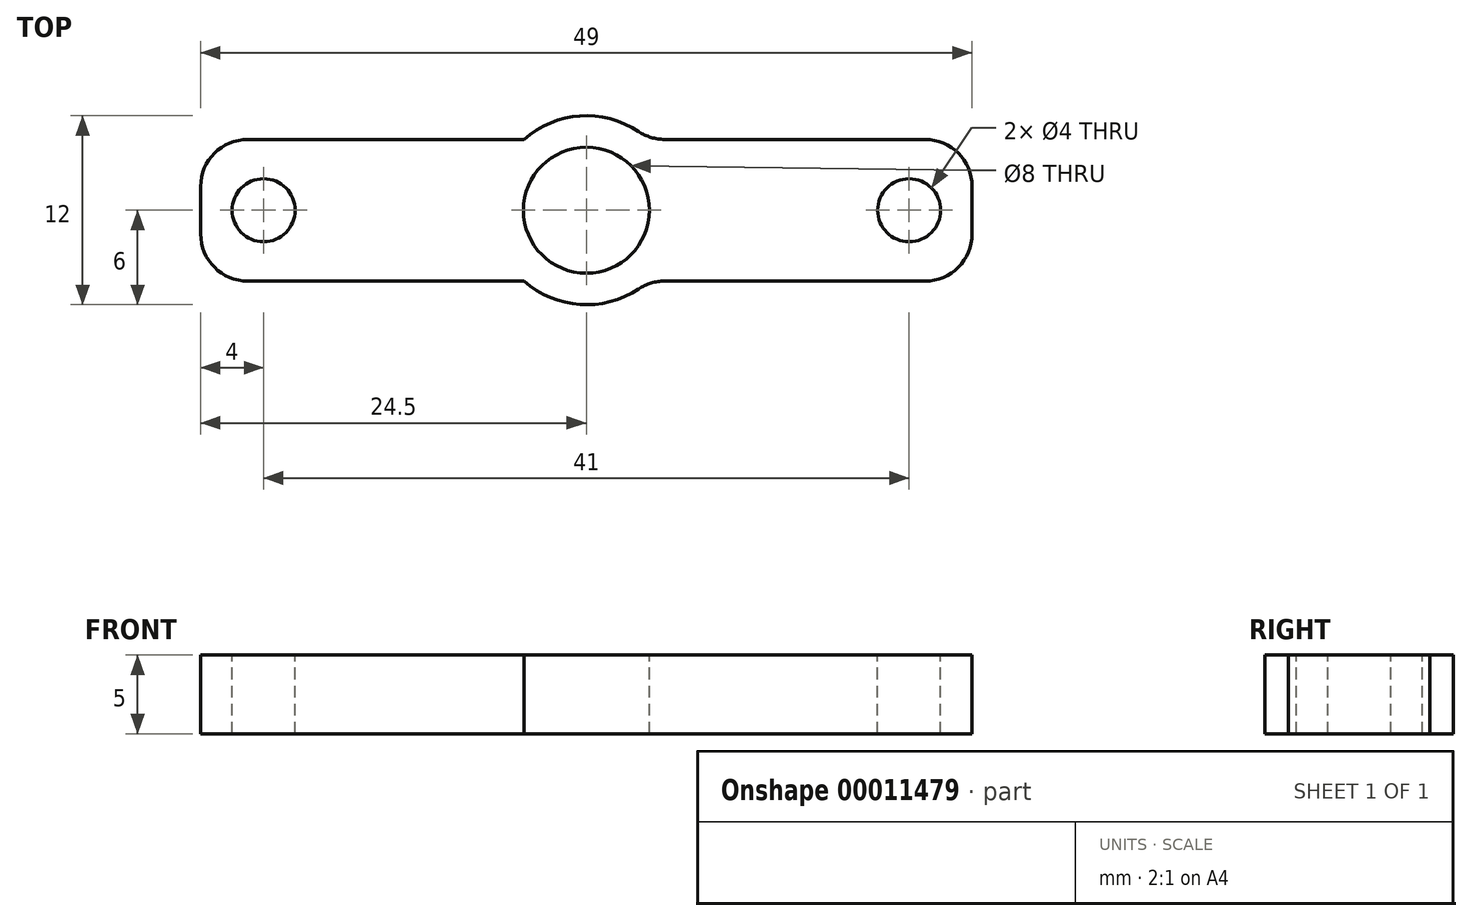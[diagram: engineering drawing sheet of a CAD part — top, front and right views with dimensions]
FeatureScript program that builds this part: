
annotation { "Feature Type Name" : "Feature", "Feature Type Description" : "" }
export const myFeature = defineFeature(function(context is Context, id is Id, definition is map)
    precondition{}
    {
        {
            var Q0;
            Q0=qCreatedBy(makeId("Top.planeOp"),FACE);
            var sketch = newSketch(context, id + "F0", { "sketchPlane" : qUnion([Q0])});
            skLineSegment(sketch, "E0.rect.bottom", {"start": v(24.5, 4.5) * mm, "end": v(3.97, 4.5) * mm});
            skLineSegment(sketch, "E0.rect.top", {"start": v(24.5, -4.5) * mm, "end": v(3.97, -4.5) * mm});
            skLineSegment(sketch, "E0.rect.left", {"start": v(24.5, 4.5) * mm, "end": v(24.5, -4.5) * mm});
            skLineSegment(sketch, "E0.rect.right", {"start": v(-24.5, 4.5) * mm, "end": v(-24.5, -4.5) * mm});
            skPoint(sketch, "E0.rect.middle", {"position": v(0, 0) * mm});
            skArc(sketch, "E1", {"start": v(-3.97, -4.5) * mm, "mid": v(0, -6) * mm, "end": v(3.97, -4.5) * mm});
            skLineSegment(sketch, "E2.trimOffspring", {"start": v(-3.97, 4.5) * mm, "end": v(-24.5, 4.5) * mm});
            skArc(sketch, "E3.trimOffspring", {"start": v(3.97, 4.5) * mm, "mid": v(0, 6) * mm, "end": v(-3.97, 4.5) * mm});
            skLineSegment(sketch, "E4.trimOffspring", {"start": v(-3.97, -4.5) * mm, "end": v(-24.5, -4.5) * mm});
            skSolve(sketch);
        }
        {
            var Q0;
            Q0 = qSketchRegion(id + "F0", true);
            extrude(context, id + "F1", {"entities" : qUnion([Q0]), "depth" : 5 * mm});
        }
        {
            var Q0;
            Q0=makeQuery(id+"F1.opExtrude","SWEPT_EDGE",EDGE,{"disambiguationData":[OSD([sQuery(id+"F0.wireOp",EDGE,"E0.rect.top"),sQuery(id+"F0.wireOp",EDGE,"E0.rect.right")])]});
            var Q1;
            Q1=makeQuery(id+"F1.opExtrude","SWEPT_EDGE",EDGE,{"disambiguationData":[OSD([sQuery(id+"F0.wireOp",EDGE,"E0.rect.bottom"),sQuery(id+"F0.wireOp",EDGE,"E0.rect.right")])]});
            var Q2;
            Q2=makeQuery(id+"F1.opExtrude","SWEPT_EDGE",EDGE,{"disambiguationData":[OSD([sQuery(id+"F0.wireOp",EDGE,"E0.rect.top"),sQuery(id+"F0.wireOp",EDGE,"E0.rect.left")])]});
            var Q3;
            Q3=makeQuery(id+"F1.opExtrude","SWEPT_EDGE",EDGE,{"disambiguationData":[OSD([sQuery(id+"F0.wireOp",EDGE,"E0.rect.bottom"),sQuery(id+"F0.wireOp",EDGE,"E0.rect.left")])]});
            fillet(context, id + "F2", {"entities" : qUnion([Q0, Q1, Q2, Q3]), "radius" : 3 * mm, "tangentPropagation" : true, "allowEdgeOverflow" : false});
        }
        {
            var Q0;
            Q0=makeQuery(id+"F1.opExtrude","CAP_FACE",FACE,{"disambiguationData":[OSD([sQuery(id+"F0.wireOp",EDGE,"E0.rect.bottom"),sQuery(id+"F0.wireOp",EDGE,"E0.rect.top"),sQuery(id+"F0.wireOp",EDGE,"E0.rect.left"),sQuery(id+"F0.wireOp",EDGE,"E0.rect.right")])],"isStart":false});
            var sketch = newSketch(context, id + "F3", { "sketchPlane" : qUnion([Q0])});
            skCircle(sketch, "E5", {"center": v(0, 0) * mm, "radius": 4 * mm});
            skSolve(sketch);
        }
        {
            var Q0;
            Q0 = qSketchRegion(id + "F3", true);
            extrude(context, id + "F4", {"entities" : qUnion([Q0]), "operationType" : NewBodyOperationType.REMOVE, "endBound" : BoundingType.THROUGH_ALL, "oppositeDirection" : true, "depth" : 25 * mm});
        }
        {
            var Q0;
            Q0=makeQuery(id+"F1.opExtrude","CAP_FACE",FACE,{"disambiguationData":[OSD([sQuery(id+"F0.wireOp",EDGE,"E0.rect.bottom"),sQuery(id+"F0.wireOp",EDGE,"E0.rect.top"),sQuery(id+"F0.wireOp",EDGE,"E0.rect.left"),sQuery(id+"F0.wireOp",EDGE,"E0.rect.right"),sQuery(id+"F0.wireOp",EDGE,"E1"),sQuery(id+"F0.wireOp",EDGE,"E2.trimOffspring"),sQuery(id+"F0.wireOp",EDGE,"E3.trimOffspring"),sQuery(id+"F0.wireOp",EDGE,"E4.trimOffspring")])],"isStart":false});
            var sketch = newSketch(context, id + "F5", { "sketchPlane" : qUnion([Q0])});
            skCircle(sketch, "E6", {"center": v(-20.5, 0) * mm, "radius": 2 * mm});
            skCircle(sketch, "E7.0.MirrorC", {"center": v(20.5, 0) * mm, "radius": 2 * mm});
            skSolve(sketch);
        }
        {
            var Q0;
            Q0 = qSketchRegion(id + "F5", true);
            extrude(context, id + "F6", {"entities" : qUnion([Q0]), "operationType" : NewBodyOperationType.REMOVE, "endBound" : BoundingType.THROUGH_ALL, "oppositeDirection" : true, "depth" : 25 * mm});
        }
    });
